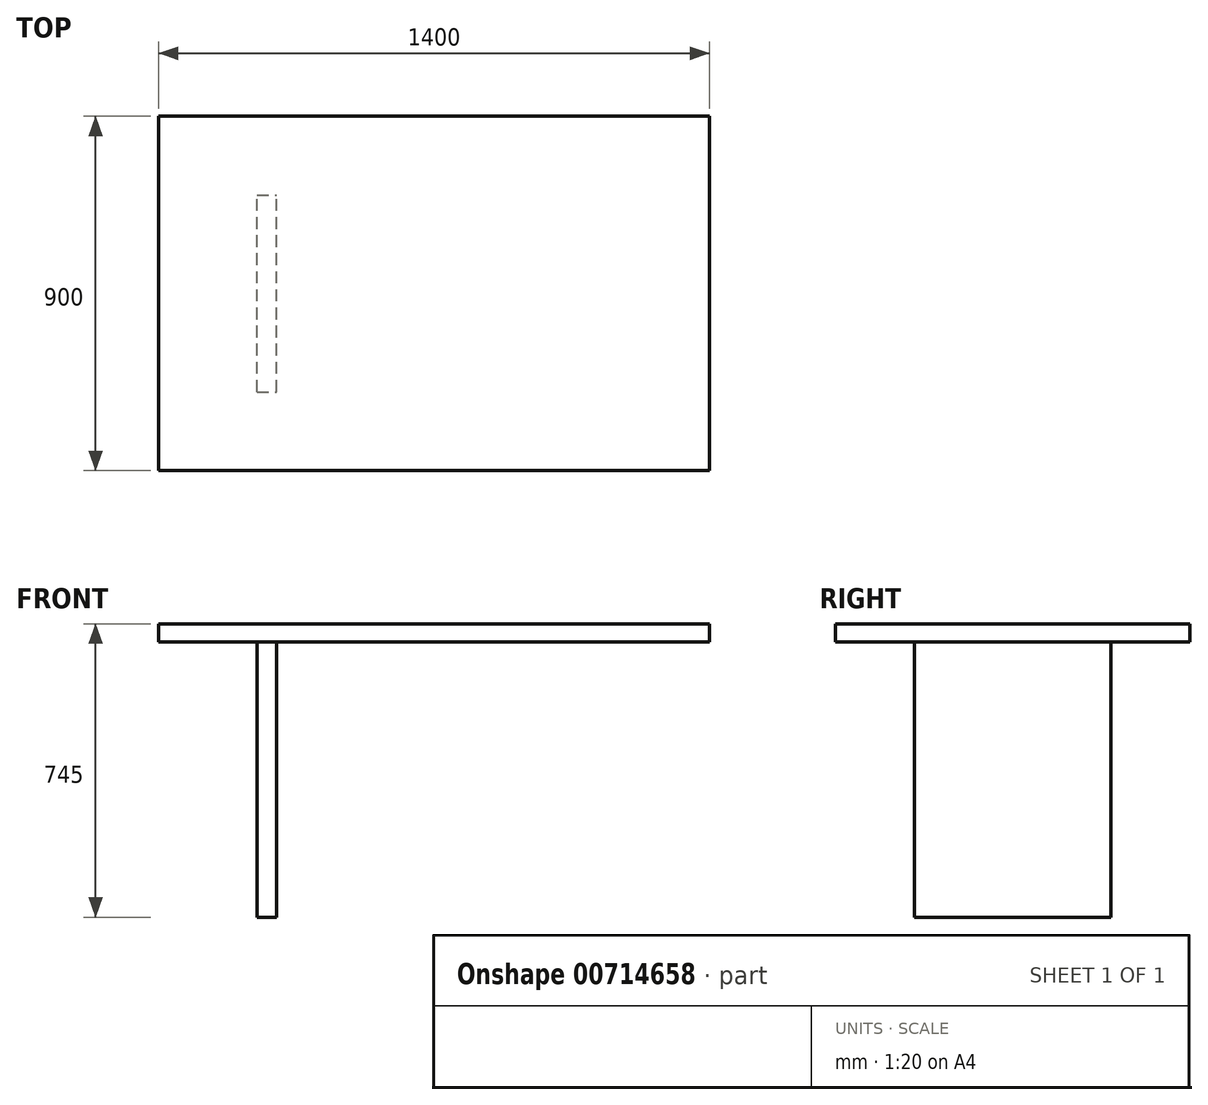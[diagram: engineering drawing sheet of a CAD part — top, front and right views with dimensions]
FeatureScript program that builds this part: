
annotation { "Feature Type Name" : "Feature", "Feature Type Description" : "" }
export const myFeature = defineFeature(function(context is Context, id is Id, definition is map)
    precondition{}
    {
        {
            var Q0;
            Q0=qCreatedBy(makeId("Top.planeOp"),FACE);
            var sketch = newSketch(context, id + "F0", { "sketchPlane" : qUnion([Q0])});
            skLineSegment(sketch, "E0.bottom", {"start": v(700, 450) * mm, "end": v(-700, 450) * mm});
            skLineSegment(sketch, "E0.top", {"start": v(700, -450) * mm, "end": v(-700, -450) * mm});
            skLineSegment(sketch, "E0.left", {"start": v(700, 450) * mm, "end": v(700, -450) * mm});
            skLineSegment(sketch, "E0.right", {"start": v(-700, 450) * mm, "end": v(-700, -450) * mm});
            skPoint(sketch, "E0.middle", {"position": v(0, 0) * mm});
            skSolve(sketch);
        }
        {
            var Q0;
            Q0=makeQuery(id+"F0.imprint","IMPRINT",FACE,{"disambiguationData":[TD([[makeQuery(id+"F0.imprint","IMPRINT",EDGE,{"derivedFrom":sQuery(id+"F0.wireOp",EDGE,"E0.bottom")}),1.0]])]});
            extrude(context, id + "F1", {"entities" : qUnion([Q0]), "depth" : 45 * mm, "offsetDistance" : 25 * mm});
        }
        {
            var Q0;
            Q0=makeQuery(id+"F1.opExtrude","CAP_FACE",FACE,{"disambiguationData":[OSD([sQuery(id+"F0.wireOp",EDGE,"E0.bottom"),sQuery(id+"F0.wireOp",EDGE,"E0.top"),sQuery(id+"F0.wireOp",EDGE,"E0.left"),sQuery(id+"F0.wireOp",EDGE,"E0.right")])],"isStart":true});
            var sketch = newSketch(context, id + "F2", { "sketchPlane" : qUnion([Q0])});
            skLineSegment(sketch, "E1.bottom", {"start": v(-450, 250) * mm, "end": v(-400, 250) * mm});
            skLineSegment(sketch, "E1.top", {"start": v(-450, -250) * mm, "end": v(-400, -250) * mm});
            skLineSegment(sketch, "E1.left", {"start": v(-450, 250) * mm, "end": v(-450, -250) * mm});
            skLineSegment(sketch, "E1.right", {"start": v(-400, 250) * mm, "end": v(-400, -250) * mm});
            skLineSegment(sketch, "E2", {"start": v(0, 0) * mm, "end": v(-400, 0) * mm, "construction": true});
            skLineSegment(sketch, "E3.MirrorCS", {"start": v(-450, -250) * mm, "end": v(-450, 250) * mm});
            skLineSegment(sketch, "E4.MirrorCS", {"start": v(450, -250) * mm, "end": v(400, -250) * mm});
            skLineSegment(sketch, "E5.MirrorCS", {"start": v(450, 250) * mm, "end": v(450, -250) * mm});
            skLineSegment(sketch, "E6.MirrorCS", {"start": v(450, -250) * mm, "end": v(450, 250) * mm});
            skLineSegment(sketch, "E7.MirrorCS", {"start": v(450, 250) * mm, "end": v(400, 250) * mm});
            skLineSegment(sketch, "E8.MirrorCS", {"start": v(400, 250) * mm, "end": v(400, -250) * mm});
            skSolve(sketch);
        }
        {
            var Q0;
            Q0=makeQuery(id+"F2.imprint","IMPRINT",FACE,{"disambiguationData":[TD([[makeQuery(id+"F2.imprint","IMPRINT",EDGE,{"derivedFrom":sQuery(id+"F2.wireOp",EDGE,"E1.bottom")}),-1.0]])]});
            var Q1;
            Q1=makeQuery(id+"F2.imprint","IMPRINT",FACE,{"disambiguationData":[TD([[makeQuery(id+"F2.imprint","IMPRINT",EDGE,{"derivedFrom":sQuery(id+"F2.wireOp",EDGE,"E6.MirrorCS")}),1.0]])]});
            extrude(context, id + "F3", {"entities" : qUnion([Q0, Q1]), "operationType" : NewBodyOperationType.ADD, "depth" : 700 * mm, "offsetDistance" : 25 * mm});
        }
    });
